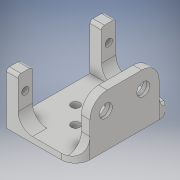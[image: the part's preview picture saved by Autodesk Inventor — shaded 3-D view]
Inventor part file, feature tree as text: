
AUTODESK INVENTOR PART (.ipt)
format: ipt  version: 2019 (Build 230136000, 136)  size: 288,256 bytes
history: native  units: mm
features: sketch x10, projected_geometry x10, extrude x6, hole x4, fillet x4
ambient origin geometry x8: Origin, YZ Plane, XZ Plane, XY Plane, X Axis, Y Axis, Z Axis, Center Point
bodies: Solid1 (feature_tree)
feature tree (34):
  extrude  "Extrusion1"  Depth=34.0mm
  extrude  "Extrusion2"  Depth=24.0mm
  extrude  "Extrusion3"  Depth=16.0mm TaperAngle=0.0deg
  hole  "Hole1"  [1 undecoded]
  hole  "Hole2"  [1 undecoded]
  extrude  "Extrusion5"  Depth=6.0mm
  extrude  "Extrusion6"  Depth=2.0mm
  hole  "Hole4"  [1 undecoded]
  fillet  "Fillet9"  Radius=6.0mm
  fillet  "Fillet10"  Radius=16.0mm
  hole  "Hole5"  [1 undecoded]
  extrude  "Extrusion7"  Depth=1.0mm
  fillet  "Fillet11"  Radius=5.0mm
  fillet  "Fillet12"  Radius=6.0mm
  sketch  "Sketch1"  dims[d0=22.0mm d1=34.0mm]
  sketch  "Sketch2"  dims[d2=18.0mm d3=0.0mm d5=24.0mm]
  projected_geometry  "Projected Loop1"
  sketch  "Sketch3"  dims[d6=3.0mm d7=16.0mm d8=0.0mm]
  sketch  "Sketch6"  dims[d9=4.0mm d10=3.0mm]
  projected_geometry  "Projected Loop3"
  sketch  "Sketch8"  dims[d11=2.0mm d12=16.0mm d13=0.0mm]
  projected_geometry  "Projected Loop5"
  sketch  "Sketch12"  dims[d15=6.0mm d16=6.0mm]
  projected_geometry  "Projected Loop8"
  projected_geometry  "Projected Loop13"
  projected_geometry  "Projected Loop14"
  sketch  "Sketch17"  dims[d18=6.0mm]
  projected_geometry  "Projected Loop15"
  sketch  "Sketch19"  dims[d20=3.0mm d21=6.0mm d22=4.0mm d23=2.0mm d24=90.0deg d25=8.0mm d26=20.594885mm d28=5.5mm]
  projected_geometry  "Projected Loop17"
  sketch  "Sketch20"  dims[d29=5.5mm d30=6.0mm d31=6.0mm]
  projected_geometry  "Projected Loop18"
  sketch  "Sketch21"  dims[d32=4.5mm d33=6.0mm d34=4.0mm d35=2.0mm d36=90.0deg d37=8.0mm d38=0.0mm d57=16.0mm d58=0.0mm d70=2.0mm d71=0.0mm d76=6.5mm d77=6.0mm d78=4.0mm d79=2.0mm d80=90.0deg d81=2.0mm d82=0.0mm d83=6.0mm d84=5.0mm d85=6.0mm d86=2.5mm d87=2.5mm d88=6.0mm d89=2.5mm d90=6.0mm d91=4.0mm d92=2.0mm d93=90.0deg d94=2.0mm d95=0.0mm d96=4.0mm d97=2.0mm d98=0.0mm d99=5.0mm d100=1.0mm d62=1.0mm d63=1.0mm d64=1.0mm d65=0.15mm d66=0.25mm d67=0.375mm d68=14.3117mm d69=0.75mm d72=0.75mm d73=0.375mm]
  projected_geometry  "Projected Loop19"
note: 4 required parameter values undecoded (feature->parameter linkage not recoverable at this tier; creation-order binding heuristic only, values carry confidence <= 0.55)
